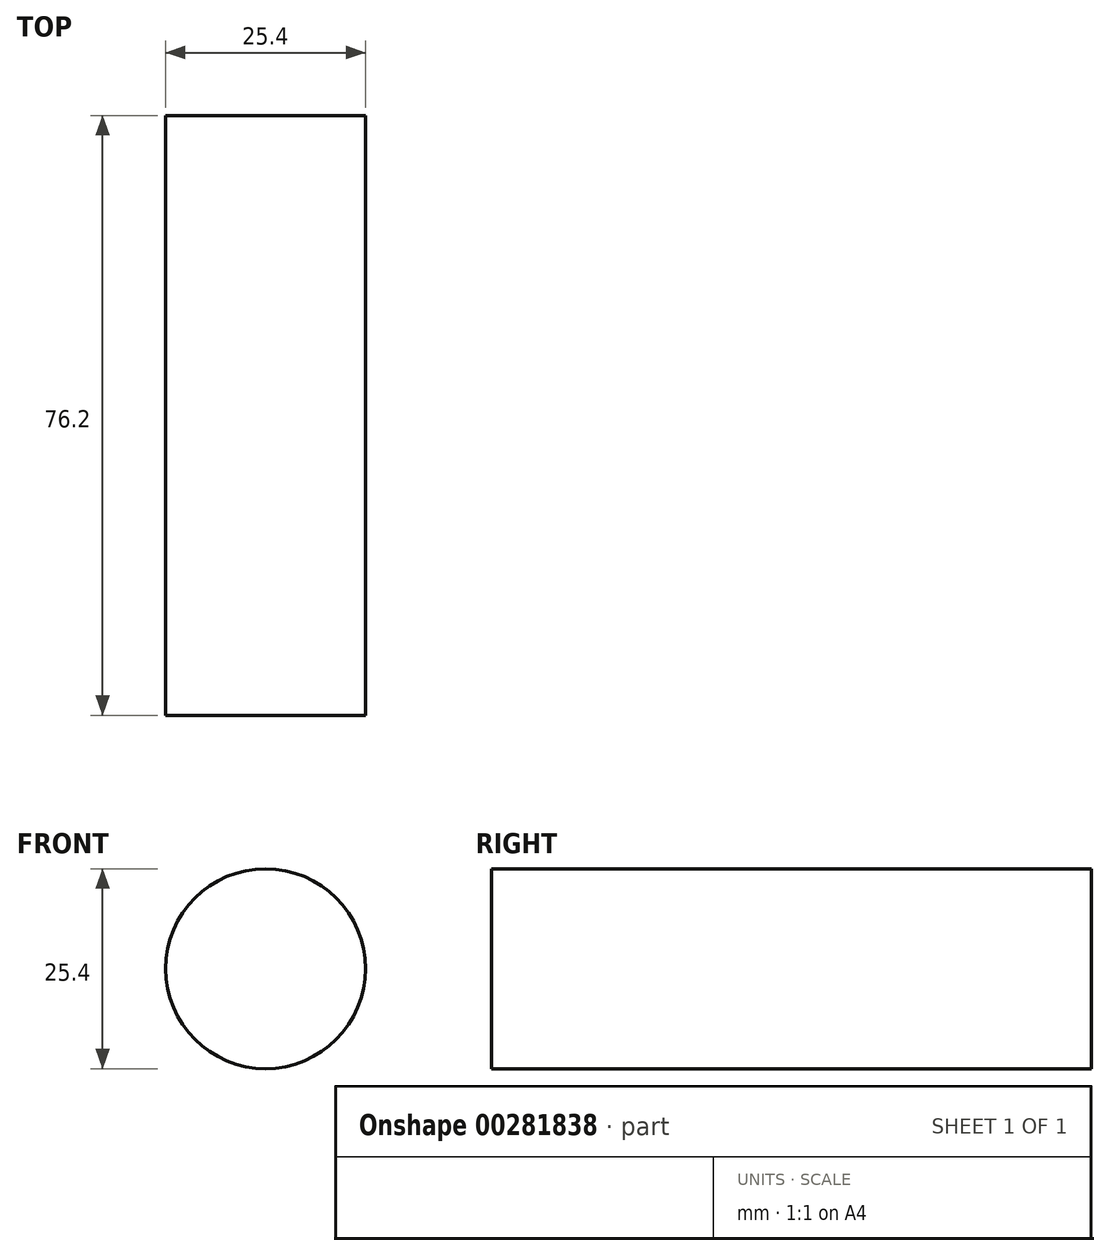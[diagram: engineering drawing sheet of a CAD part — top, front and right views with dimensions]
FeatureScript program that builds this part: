
annotation { "Feature Type Name" : "Feature", "Feature Type Description" : "" }
export const myFeature = defineFeature(function(context is Context, id is Id, definition is map)
    precondition{}
    {
        {
            var Q0;
            Q0=qCreatedBy(makeId("Front.planeOp"),FACE);
            var sketch = newSketch(context, id + "F0", { "sketchPlane" : qUnion([Q0])});
            skCircle(sketch, "E0", {"center": v(-42.2, 45.45) * mm, "radius": 12.7 * mm});
            skSolve(sketch);
        }
        {
            var Q0;
            Q0 = qSketchRegion(id + "F0", true);
            extrude(context, id + "F1", {"entities" : qUnion([Q0]), "depth" : 76.2 * mm});
        }
    });
